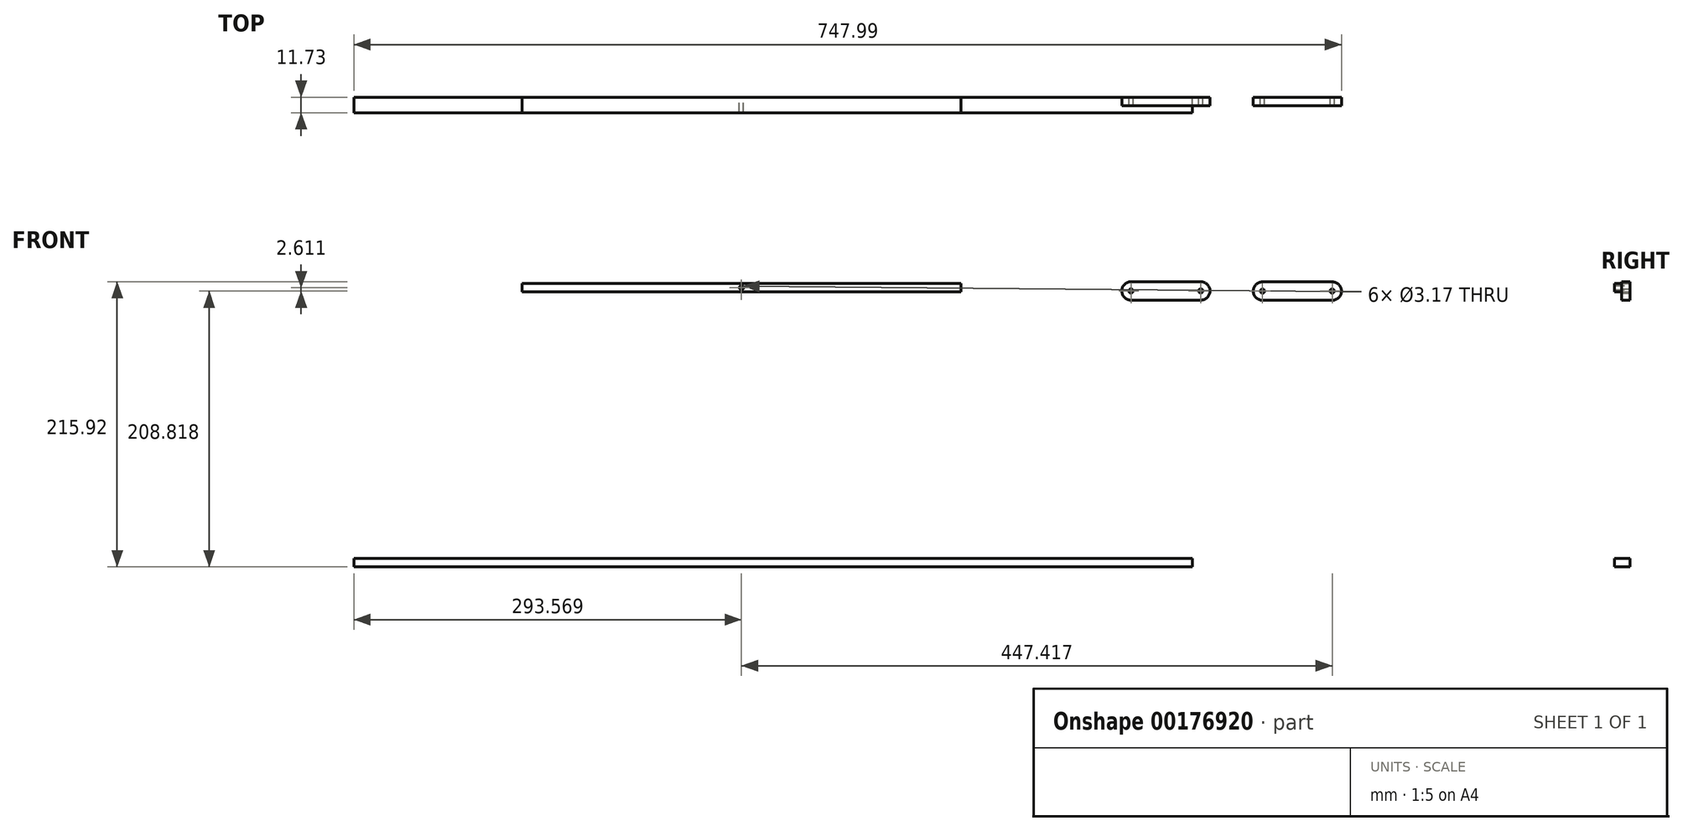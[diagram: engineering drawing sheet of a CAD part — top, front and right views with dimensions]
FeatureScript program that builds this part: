
annotation { "Feature Type Name" : "Feature", "Feature Type Description" : "" }
export const myFeature = defineFeature(function(context is Context, id is Id, definition is map)
    precondition{}
    {
        {
            var Q0;
            Q0=qCreatedBy(makeId("Front.planeOp"),FACE);
            var sketch = newSketch(context, id + "F0", { "sketchPlane" : qUnion([Q0])});
            skLineSegment(sketch, "E0.bottom", {"start": v(-373.69, -26.05) * mm, "end": v(261.31, -26.05) * mm});
            skLineSegment(sketch, "E0.top", {"start": v(-373.69, -32.4) * mm, "end": v(261.31, -32.4) * mm});
            skLineSegment(sketch, "E0.left", {"start": v(-373.69, -26.05) * mm, "end": v(-373.69, -32.4) * mm});
            skLineSegment(sketch, "E0.right", {"start": v(261.31, -26.05) * mm, "end": v(261.31, -32.4) * mm});
            skLineSegment(sketch, "E1.bottom", {"start": v(-246.19, 182.2) * mm, "end": v(85.94, 182.2) * mm});
            skLineSegment(sketch, "E1.top", {"start": v(-246.19, 175.85) * mm, "end": v(85.94, 175.85) * mm});
            skLineSegment(sketch, "E1.left", {"start": v(-246.19, 182.2) * mm, "end": v(-246.19, 175.85) * mm});
            skLineSegment(sketch, "E1.right", {"start": v(85.94, 182.2) * mm, "end": v(85.94, 175.85) * mm});
            skLineSegment(sketch, "E2", {"start": v(-80.12, 175.85) * mm, "end": v(-80.12, 182.2) * mm, "construction": true});
            skLineSegment(sketch, "E3", {"start": v(-246.19, 179.03) * mm, "end": v(85.94, 179.03) * mm, "construction": true});
            skCircle(sketch, "E4", {"center": v(-80.12, 179.03) * mm, "radius": 1.59 * mm});
            skSolve(sketch);
        }
        {
            var Q0;
            Q0 = qSketchRegion(id + "F0", true);
            extrude(context, id + "F1", {"entities" : qUnion([Q0]), "depth" : 11.73 * mm});
        }
        {
            var Q0;
            Q0 = qSketchRegion(id + "F0", true);
            extrude(context, id + "F2", {"entities" : qUnion([Q0]), "depth" : 11.73 * mm});
        }
        {
            var Q0;
            Q0=qCreatedBy(makeId("Front.planeOp"),FACE);
            var sketch = newSketch(context, id + "F3", { "sketchPlane" : qUnion([Q0])});
            skLineSegment(sketch, "E5", {"start": v(214.9, 183.52) * mm, "end": v(267.73, 183.52) * mm});
            skLineSegment(sketch, "E6", {"start": v(214.9, 169.5) * mm, "end": v(267.73, 169.5) * mm});
            skArc(sketch, "E7", {"start": v(214.9, 183.52) * mm, "mid": v(207.89, 176.51) * mm, "end": v(214.9, 169.5) * mm});
            skArc(sketch, "E8", {"start": v(267.73, 169.5) * mm, "mid": v(274.73, 176.51) * mm, "end": v(267.73, 183.52) * mm});
            skLineSegment(sketch, "E9", {"start": v(314.46, 183.42) * mm, "end": v(367.3, 183.42) * mm});
            skLineSegment(sketch, "E10", {"start": v(314.46, 169.41) * mm, "end": v(367.3, 169.41) * mm});
            skArc(sketch, "E11", {"start": v(314.46, 183.42) * mm, "mid": v(307.46, 176.42) * mm, "end": v(314.46, 169.41) * mm});
            skArc(sketch, "E12", {"start": v(367.3, 169.41) * mm, "mid": v(374.3, 176.42) * mm, "end": v(367.3, 183.42) * mm});
            skCircle(sketch, "E13", {"center": v(214.9, 176.51) * mm, "radius": 1.59 * mm});
            skCircle(sketch, "E14", {"center": v(267.73, 176.51) * mm, "radius": 1.59 * mm});
            skCircle(sketch, "E15", {"center": v(314.46, 176.42) * mm, "radius": 1.59 * mm});
            skCircle(sketch, "E16", {"center": v(367.3, 176.42) * mm, "radius": 1.59 * mm});
            skSolve(sketch);
        }
        {
            var Q0;
            Q0 = qSketchRegion(id + "F3", true);
            extrude(context, id + "F4", {"entities" : qUnion([Q0]), "depth" : 6.35 * mm});
        }
    });
